# Revit family: Reception-Teknion-B_CRL_Reception_Desk_Module-L_Shaped-R2019
name_source: partatom
category: Furniture
units: mm (PartAtom-declared; Revit-internal decimal feet)

## family parameters
Always vertical = Yes
Cut with Voids When Loaded = No
OmniClass Number = 23.40.20.00
OmniClass Title = General Furniture and Specialties
Room Calculation Point = No
Shared = Yes
Work Plane-Based = No

## types (2) — shared parameters
Assembly Code = E2020200
Manufacturer = Teknion
Manufacturer Fax = 416.661.4586
Part Number = B_CRL
Product Documentation Link = https://www.teknion.com
Product Line = Expansion Casegoods
Product Page URL = https://www.teknion.com
Series = Expansion Casegoods
Sustainability Data = https://www.teknion.com
URL = www.teknion.com
Unit Weight URL = http://www.teknion.com
Warranty = http://www.teknion.com

## per-type parameters (varying)
| type | 1-3/16" Thick WS | Description | Gable Thickness | Model | Worksurface Thickness |
| 1-3/16" Thick WS, 12" Depth | Yes | Reception Desk Module – L-Shaped, 1-3/16" Worksurface Thickness, 12" Depth | 1.016 " | BMCRL12_____ | 1.189 " |
| 1-9/16" Thick WS, 12" Depth | No | Reception Desk Module – L-Shaped, 1-9/16" Worksurface Thickness, 12" Depth | 1.512 " | BXCRL12_____ | 1.555 " |

## geometry (parser evidence)
native form markers: Sweep x3
no freeform markers — native parametric forms only
